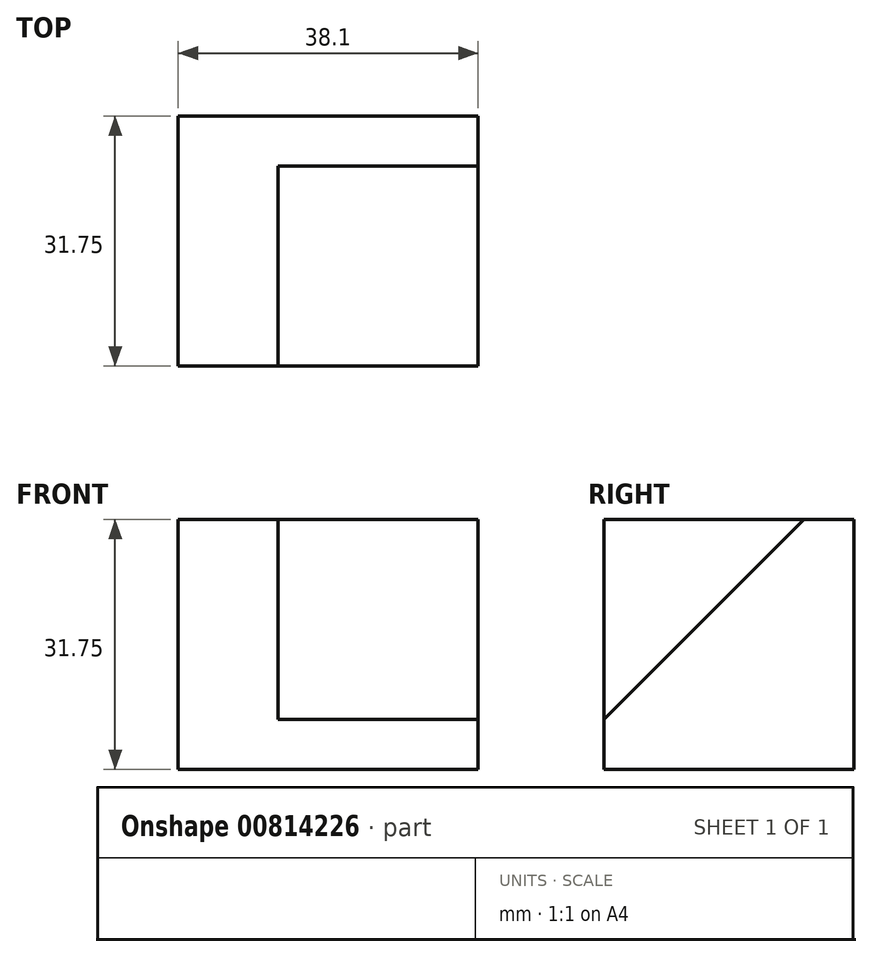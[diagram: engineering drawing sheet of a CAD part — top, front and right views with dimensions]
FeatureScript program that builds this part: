
annotation { "Feature Type Name" : "Feature", "Feature Type Description" : "" }
export const myFeature = defineFeature(function(context is Context, id is Id, definition is map)
    precondition{}
    {
        {
            var Q0;
            Q0=qCreatedBy(makeId("Top.planeOp"),FACE);
            var sketch = newSketch(context, id + "F0", { "sketchPlane" : qUnion([Q0])});
            skLineSegment(sketch, "E0.bottom", {"start": v(0, 0) * mm, "end": v(38.1, 0) * mm});
            skLineSegment(sketch, "E0.top", {"start": v(0, 31.75) * mm, "end": v(38.1, 31.75) * mm});
            skLineSegment(sketch, "E0.left", {"start": v(0, 0) * mm, "end": v(0, 31.75) * mm});
            skLineSegment(sketch, "E0.right", {"start": v(38.1, 0) * mm, "end": v(38.1, 31.75) * mm});
            skSolve(sketch);
        }
        {
            var Q0;
            Q0=makeQuery(id+"F0.imprint","IMPRINT",FACE,{"disambiguationData":[TD([[makeQuery(id+"F0.imprint","IMPRINT",EDGE,{"derivedFrom":sQuery(id+"F0.wireOp",EDGE,"E0.bottom")}),1.0]])]});
            extrude(context, id + "F1", {"entities" : qUnion([Q0]), "depth" : 31.75 * mm, "offsetDistance" : 25.4 * mm});
        }
        {
            var Q0;
            Q0=makeQuery(id+"F1.opExtrude","SWEPT_FACE",FACE,{"disambiguationData":[OSD([sQuery(id+"F0.wireOp",EDGE,"E0.right")])]});
            var sketch = newSketch(context, id + "F2", { "sketchPlane" : qUnion([Q0])});
            skLineSegment(sketch, "E1", {"start": v(31.75, 31.75) * mm, "end": v(25.4, 31.75) * mm});
            skLineSegment(sketch, "E2", {"start": v(0, 0) * mm, "end": v(0, 6.35) * mm});
            skLineSegment(sketch, "E3", {"start": v(25.4, 31.75) * mm, "end": v(0, 6.35) * mm});
            skSolve(sketch);
        }
        {
            var Q0;
            {var subQ0=sQuery(id+"F2.wireOp",EDGE,"E3");Q0=makeQuery(id+"F2.imprint","IMPRINT",FACE,{"disambiguationData":[TD([[makeQuery(id+"F2.imprint","IMPRINT",EDGE,{"derivedFrom":subQ0}),-1.0]])]});}
            extrude(context, id + "F3", {"entities" : qUnion([Q0]), "operationType" : NewBodyOperationType.REMOVE, "oppositeDirection" : true, "depth" : 25.4 * mm, "offsetDistance" : 25.4 * mm});
        }
    });
